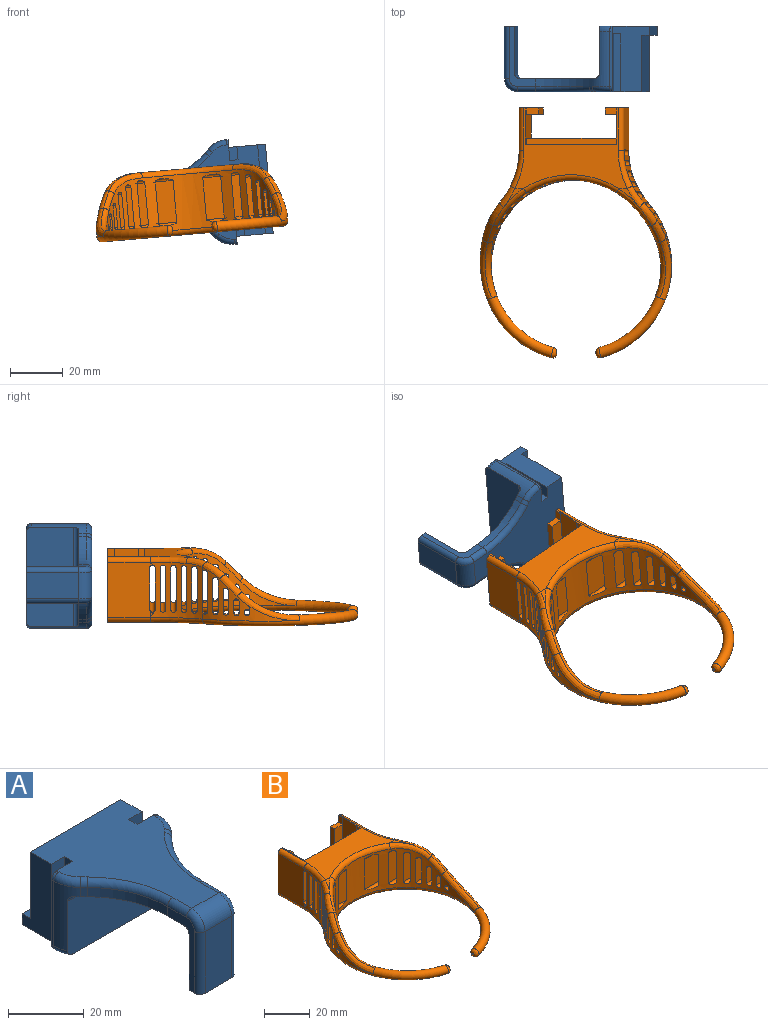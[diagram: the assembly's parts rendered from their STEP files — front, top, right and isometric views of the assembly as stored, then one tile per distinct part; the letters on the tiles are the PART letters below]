
ASSEMBLY  parts=2 mates=1
PART A: 61 faces, bbox 41.6x56.9x25.4 mm
  f0: plane 20x10mm, normal (0,-1,0), area 200mm2, adj f31,f34,f49,f50
  f1: plane 18x14mm, normal (0,1,0), area 252mm2, adj f2,f3,f31,f32
  f2: plane 23x10.07mm, normal (1,0,0), area 69.1mm2, adj f1,f6,f31,f32,f40,f47,f48,f49
  f3: plane 23x10.07mm, normal (-1,0,0), area 69.1mm2, adj f1,f6,f31,f32,f39,f50,f51,f52
  f4: plane 48.5x36mm, normal (0,0,1), area 1036.4mm2, adj f5,f7,f8,f10,f11,f12,f13,f14
  f5: plane 25x14.06mm, normal (-1,0,0), area 218.4mm2, adj f4,f8,f9,f12,f14,f18,f27,f28
  f6: plane 35.78x29.5mm, normal (0,0,-1), area 572.7mm2, adj f2,f3,f32,f33,f37,f38,f39,f40
  f7: plane 25x14.06mm, normal (1,0,0), area 218.4mm2, adj f4,f8,f9,f13,f15,f17,f27,f28
  f8: plane 34x21.5mm, normal (0,1,0), area 731mm2, adj f4,f5,f7,f27
  f9: plane 36x19mm, normal (0,0,-1), area 542.3mm2, adj f5,f7,f12,f13,f16,f19,f20,f21
  f10: plane 22x3.12mm, normal (1,0,0), area 68.6mm2, adj f4,f13,f15,f17
  f11: plane 22x3.12mm, normal (-1,0,0), area 68.6mm2, adj f4,f12,f14,f18
  f12: plane 25x8mm, normal (0,1,0), area 183.3mm2, adj f4,f5,f9,f11,f18,f36,f56,f58
  f13: plane 25x8mm, normal (0,1,0), area 183.3mm2, adj f4,f7,f9,f10,f17,f35,f43,f60
  f14: plane 22x5mm, normal (0,-1,0), area 110mm2, adj f4,f5,f11,f18
  f15: plane 22x5mm, normal (0,-1,0), area 110mm2, adj f4,f7,f10,f17
  f16: plane 38.2x18mm, normal (0,-1,0), area 685.8mm2, adj f9,f33,f41,f42,f57,f59
  f17: plane 5x3.12mm, normal (0,0,1), area 15.6mm2, adj f7,f10,f13,f15
  f18: plane 5x3.12mm, normal (0,0,1), area 15.6mm2, adj f5,f11,f12,f14
  f19: plane 22x18mm, normal (0,-1,0), area 396mm2, adj f9,f20,f22,f29
  f20: plane 22x3.12mm, normal (1,0,0), area 68.6mm2, adj f9,f19,f21,f29
  f21: plane 22x18mm, normal (0,1,0), area 396mm2, adj f9,f20,f22,f29
  f22: plane 22x3.12mm, normal (-1,0,0), area 68.6mm2, adj f9,f19,f21,f29
  f23: plane 28x22mm, normal (0,-1,0), area 616mm2, adj f9,f24,f26,f30
  f24: plane 22x1.94mm, normal (1,0,0), area 42.7mm2, adj f9,f23,f25,f30
  f25: plane 28x22mm, normal (0,1,0), area 616mm2, adj f9,f24,f26,f30
  f26: plane 22x1.94mm, normal (-1,0,0), area 42.7mm2, adj f9,f23,f25,f30
  f27: plane 34x3mm, normal (0,0,1), area 102mm2, adj f5,f7,f8,f28
  f28: plane 34x3.5mm, normal (0,1,0), area 119mm2, adj f5,f7,f9,f27
  f29: plane 18x3.12mm, normal (0,0,-1), area 56.2mm2, adj f19,f20,f21,f22
  f30: plane 28x1.94mm, normal (0,0,-1), area 54.3mm2, adj f23,f24,f25,f26
  f31: plane 14x4mm, normal (0,0,-1), area 54.3mm2, adj f0,f1,f2,f3,f49,f50
  f32: cylinder r=2mm len=14mm, axis (-1,0,0), area 44mm2, adj f1,f2,f3,f6
  f33: cylinder r=2mm len=38.2mm, axis (1,0,0), area 117.5mm2, adj f6,f16,f41,f42
  f34: cylinder r=5mm len=10mm, axis (-1,0,0), area 78.5mm2, adj f0,f4,f48,f51
  f35: plane 21x0.8mm, normal (1,0,0), area 16.8mm2, adj f13,f42,f43,f60
  f36: plane 21x0.8mm, normal (-1,0,0), area 16.8mm2, adj f12,f41,f56,f58
  f37: plane 3x1.28mm, normal (0.71,-0.71,0), area 5.4mm2, adj f6,f40,f42,f45
  f38: plane 3x1.28mm, normal (-0.71,-0.71,0), area 5.4mm2, adj f6,f39,f41,f54
  f39: cylinder r=30mm len=21.21mm, axis (0,0,1), area 70.7mm2, adj f3,f6,f38,f53
  f40: cylinder r=30mm len=21.21mm, axis (0,0,-1), area 70.7mm2, adj f2,f6,f37,f46
  f41: cylinder r=10mm len=21mm, axis (0,0,-1), area 101.4mm2, adj f6,f16,f33,f36,f38,f55,f57
  f42: cylinder r=10mm len=21mm, axis (0,0,-1), area 101.4mm2, adj f6,f16,f33,f35,f37,f44,f59
  f43: cylinder r=2mm len=2mm, axis (0,-1,0), area 2.5mm2, adj f4,f13,f35,f44
  f44: torus R=8mm, axis (0,0,1), area 22.9mm2, adj f4,f42,f43,f45
  f45: cylinder r=2mm len=2.7mm, axis (0.71,0.71,0), area 5.7mm2, adj f4,f37,f44,f46
  f46: torus R=32mm, axis (0,0,1), area 75.8mm2, adj f4,f40,f45,f47
  f47: cylinder r=2mm len=7.07mm, axis (0,-1,0), area 22.2mm2, adj f2,f4,f46,f48
  f48: torus R=3mm, axis (1,0,0), area 21.1mm2, adj f2,f34,f47,f49
  f49: cylinder r=2mm len=20mm, axis (0,0,-1), area 62.8mm2, adj f0,f2,f31,f48
  f50: cylinder r=2mm len=20mm, axis (0,0,-1), area 62.8mm2, adj f0,f3,f31,f51
  f51: torus R=3mm, axis (-1,0,0), area 21.1mm2, adj f3,f34,f50,f52
  f52: cylinder r=2mm len=7.07mm, axis (0,-1,0), area 22.2mm2, adj f3,f4,f51,f53
  f53: torus R=32mm, axis (0,0,1), area 75.8mm2, adj f4,f39,f52,f54
  f54: cylinder r=2mm len=2.7mm, axis (0.71,-0.71,0), area 5.7mm2, adj f4,f38,f53,f55
  f55: torus R=8mm, axis (0,0,1), area 22.9mm2, adj f4,f41,f54,f56
  f56: cylinder r=2mm len=2mm, axis (0,-1,0), area 2.5mm2, adj f4,f12,f36,f55
  f57: torus R=8mm, axis (0,0,1), area 13.5mm2, adj f9,f16,f41,f58
  f58: cylinder r=2mm len=2mm, axis (0,-1,0), area 2.5mm2, adj f9,f12,f36,f57
  f59: torus R=8mm, axis (0,0,1), area 13.5mm2, adj f9,f16,f42,f60
  f60: cylinder r=2mm len=2mm, axis (0,-1,0), area 2.5mm2, adj f9,f13,f35,f59
PART B: 124 faces, bbox 79x98.1x25.1 mm
  f0: cylinder r=36.5mm len=37.21mm, axis (0,0,-1), area 194.9mm2, adj f7,f74,f75,f76,f77,f78,f79,f80
  f1: cylinder r=32.5mm len=65mm, axis (0,0,-1), area 1086.7mm2, adj f28,f29,f30,f31,f32,f33,f34,f35
  f2: cylinder r=36.5mm len=37.21mm, axis (0,0,-1), area 194.9mm2, adj f6,f56,f57,f58,f59,f60,f61,f62
  f3: plane 43.01x30.72mm, normal (0,0,1), area 521.3mm2, adj f8,f9,f10,f13,f15,f18,f19,f21
  f4: plane 0.83x0.8mm, normal (-1,0,0), area 0.5mm2, adj f119
  f5: plane 0.83x0.8mm, normal (1,0,0), area 0.5mm2, adj f118
  f6: cylinder r=30mm len=21mm, axis (0,0,-1), area 264.7mm2, adj f2,f16,f36,f37,f38,f39,f40,f41
  f7: cylinder r=30mm len=21mm, axis (0,0,-1), area 264.7mm2, adj f0,f17,f28,f29,f30,f31,f32,f33
  f8: plane 25x7.25mm, normal (0,1,0), area 162.2mm2, adj f3,f11,f14,f17,f22,f23,f94,f109
  f9: plane 35x25mm, normal (0,1,0), area 744.7mm2, adj f3,f14,f18,f19,f24,f25,f26
  f10: plane 25x4.75mm, normal (0,-1,0), area 101.4mm2, adj f3,f11,f14,f18,f22,f23
  f11: plane 21.25x2.5mm, normal (1,0,0), area 53.1mm2, adj f8,f10,f14,f22
  f12: plane 21.25x2.5mm, normal (-1,0,0), area 53.1mm2, adj f13,f14,f15,f20
  f13: plane 25x7.25mm, normal (0,1,0), area 162.2mm2, adj f3,f12,f14,f16,f20,f21,f101,f107
  f14: plane 51.88x37.25mm, normal (0,0,-1), area 645.1mm2, adj f8,f9,f10,f11,f12,f13,f15,f18
  f15: plane 25x4.75mm, normal (0,-1,0), area 101.4mm2, adj f3,f12,f14,f19,f20,f21
  f16: plane 21x16.16mm, normal (1,0,0), area 336.7mm2, adj f6,f13,f44,f45,f47,f101,f107
  f17: plane 21x16.16mm, normal (-1,0,0), area 336.7mm2, adj f7,f8,f44,f45,f47,f94,f109
  f18: plane 25x9mm, normal (1,0,0), area 225mm2, adj f3,f9,f10,f14
  f19: plane 25x9mm, normal (-1,0,0), area 225mm2, adj f3,f9,f14,f15
  f20: plane 4.63x2.5mm, normal (0,0,1), area 11.6mm2, adj f12,f13,f15,f21
  f21: plane 3.75x2.5mm, normal (-1,0,0), area 9.4mm2, adj f3,f13,f15,f20
  f22: plane 4.63x2.5mm, normal (0,0,1), area 11.6mm2, adj f8,f10,f11,f23
  f23: plane 3.75x2.5mm, normal (1,0,0), area 9.4mm2, adj f3,f8,f10,f22
  f24: plane 34.75x2.5mm, normal (0,0,1), area 86.9mm2, adj f9,f25,f26,f27
  f25: plane 3.75x2.5mm, normal (1,0,0), area 9.4mm2, adj f3,f9,f24,f27
  f26: plane 3.75x2.5mm, normal (-1,0,0), area 9.4mm2, adj f3,f9,f24,f27
  f27: plane 34.75x3.75mm, normal (0,1,0), area 130.3mm2, adj f3,f24,f25,f26
  f28: cylinder r=1mm len=9.38mm, axis (1,0,0), area 22.6mm2, adj f1,f7,f29,f31
  f29: plane 16x8.03mm, normal (0,-1,0), area 128.4mm2, adj f1,f7,f28,f30
  f30: cylinder r=1mm len=9.38mm, axis (1,0,0), area 22.6mm2, adj f1,f7,f29,f31
  f31: plane 16x6.38mm, normal (0,1,0), area 102.1mm2, adj f1,f7,f28,f30
  f32: plane 16.76x16mm, normal (0,-1,0), area 268.1mm2, adj f1,f7,f33,f35
  f33: cylinder r=1mm len=17.71mm, axis (1,0,0), area 43.4mm2, adj f1,f7,f32,f34
  f34: plane 16x10.89mm, normal (0,1,0), area 174.2mm2, adj f1,f7,f33,f35
  f35: cylinder r=1mm len=17.71mm, axis (1,0,0), area 43.4mm2, adj f1,f7,f32,f34
  f36: plane 43.32x16mm, normal (0,1,0), area 693.1mm2, adj f6,f7,f37,f39
  f37: cylinder r=1mm len=43.32mm, axis (1,0,0), area 134.2mm2, adj f6,f7,f36,f38
  f38: plane 42.09x16mm, normal (0,-1,0), area 673.4mm2, adj f6,f7,f37,f39
  f39: cylinder r=1mm len=43.32mm, axis (1,0,0), area 134.2mm2, adj f6,f7,f36,f38
  f40: cylinder r=1mm len=41.15mm, axis (1,0,0), area 128.2mm2, adj f6,f7,f41,f43
  f41: plane 41.15x16mm, normal (0,1,0), area 658.4mm2, adj f6,f7,f40,f42
  f42: cylinder r=1mm len=41.15mm, axis (1,0,0), area 128.2mm2, adj f6,f7,f41,f43
  f43: plane 40.49x16mm, normal (0,-1,0), area 647.9mm2, adj f6,f7,f40,f42
  f44: plane 40x16mm, normal (0,-1,0), area 640mm2, adj f16,f17,f45,f47
  f45: cylinder r=1mm len=40.11mm, axis (1,0,0), area 125.8mm2, adj f6,f7,f16,f17,f44,f46
  f46: plane 40.11x16mm, normal (0,1,0), area 641.8mm2, adj f6,f7,f45,f47
  f47: cylinder r=1mm len=40.11mm, axis (1,0,0), area 125.8mm2, adj f6,f7,f16,f17,f44,f46
  f48: plane 16x6.38mm, normal (0,1,0), area 102.1mm2, adj f1,f6,f49,f51
  f49: cylinder r=1mm len=9.38mm, axis (1,0,0), area 22.6mm2, adj f1,f6,f48,f50
  f50: plane 16x8.03mm, normal (0,-1,0), area 128.4mm2, adj f1,f6,f49,f51
  f51: cylinder r=1mm len=9.38mm, axis (1,0,0), area 22.6mm2, adj f1,f6,f48,f50
  f52: cylinder r=1mm len=17.71mm, axis (1,0,0), area 43.4mm2, adj f1,f6,f53,f55
  f53: plane 16x10.89mm, normal (0,1,0), area 174.2mm2, adj f1,f6,f52,f54
  f54: cylinder r=1mm len=17.71mm, axis (1,0,0), area 43.4mm2, adj f1,f6,f53,f55
  f55: plane 16.76x16mm, normal (0,-1,0), area 268.1mm2, adj f1,f6,f52,f54
  f56: plane 4.11x0.34mm, normal (0,-1,0), area 1.4mm2, adj f1,f2,f120,f121
  f57: plane 4.06x0.34mm, normal (0,1,0), area 1.4mm2, adj f1,f2,f120,f121
  f58: plane 4.34x4.18mm, normal (0,1,0), area 18.2mm2, adj f1,f2,f59,f61
  f59: cylinder r=1mm len=4.9mm, axis (1,0,0), area 13.3mm2, adj f1,f2,f58,f60
  f60: plane 4.34x4.27mm, normal (0,-1,0), area 18.5mm2, adj f1,f2,f59,f61
  f61: cylinder r=1mm len=4.9mm, axis (1,0,0), area 13.3mm2, adj f1,f2,f58,f60
  f62: plane 8.34x4.52mm, normal (0,-1,0), area 37.7mm2, adj f1,f2,f63,f65
  f63: cylinder r=1mm len=5.42mm, axis (1,0,0), area 14mm2, adj f1,f2,f62,f64
  f64: plane 8.34x4.38mm, normal (0,1,0), area 36.5mm2, adj f1,f2,f63,f65
  f65: cylinder r=1mm len=5.42mm, axis (1,0,0), area 14mm2, adj f1,f2,f62,f64
  f66: cylinder r=1mm len=6.14mm, axis (1,0,0), area 15.1mm2, adj f1,f2,f67,f69
  f67: plane 12.34x4.92mm, normal (0,-1,0), area 60.7mm2, adj f1,f2,f66,f68
  f68: cylinder r=1mm len=6.14mm, axis (1,0,0), area 15.1mm2, adj f1,f2,f67,f69
  f69: plane 12.34x4.69mm, normal (0,1,0), area 57.9mm2, adj f1,f2,f66,f68
  f70: plane 14.81x5.59mm, normal (0,-1,0), area 82.7mm2, adj f1,f2,f71,f73
  f71: cylinder r=1mm len=7.21mm, axis (1,0,0), area 16.9mm2, adj f1,f2,f70,f72
  f72: plane 14.81x5.2mm, normal (0,1,0), area 77.1mm2, adj f1,f2,f71,f73
  f73: cylinder r=1mm len=7.21mm, axis (1,0,0), area 16.9mm2, adj f1,f2,f70,f72
  f74: plane 4.06x0.34mm, normal (0,1,0), area 1.4mm2, adj f0,f1,f122,f123
  f75: plane 4.11x0.34mm, normal (0,-1,0), area 1.4mm2, adj f0,f1,f122,f123
  f76: cylinder r=1mm len=4.9mm, axis (1,0,0), area 13.3mm2, adj f0,f1,f77,f79
  f77: plane 4.34x4.27mm, normal (0,-1,0), area 18.5mm2, adj f0,f1,f76,f78
  f78: cylinder r=1mm len=4.9mm, axis (1,0,0), area 13.3mm2, adj f0,f1,f77,f79
  f79: plane 4.34x4.18mm, normal (0,1,0), area 18.2mm2, adj f0,f1,f76,f78
  f80: cylinder r=1mm len=5.42mm, axis (1,0,0), area 14mm2, adj f0,f1,f81,f83
  f81: plane 8.34x4.38mm, normal (0,1,0), area 36.5mm2, adj f0,f1,f80,f82
  f82: cylinder r=1mm len=5.42mm, axis (1,0,0), area 14mm2, adj f0,f1,f81,f83
  f83: plane 8.34x4.52mm, normal (0,-1,0), area 37.7mm2, adj f0,f1,f80,f82
  f84: plane 12.34x4.69mm, normal (0,1,0), area 57.9mm2, adj f0,f1,f85,f87
  f85: cylinder r=1mm len=6.14mm, axis (1,0,0), area 15.1mm2, adj f0,f1,f84,f86
  f86: plane 12.34x4.92mm, normal (0,-1,0), area 60.7mm2, adj f0,f1,f85,f87
  f87: cylinder r=1mm len=6.14mm, axis (1,0,0), area 15.1mm2, adj f0,f1,f84,f86
  f88: cylinder r=1mm len=7.21mm, axis (1,0,0), area 16.9mm2, adj f0,f1,f89,f91
  f89: plane 14.81x5.2mm, normal (0,1,0), area 77.1mm2, adj f0,f1,f88,f90
  f90: cylinder r=1mm len=7.21mm, axis (1,0,0), area 16.9mm2, adj f0,f1,f89,f91
  f91: plane 14.81x5.59mm, normal (0,-1,0), area 82.7mm2, adj f0,f1,f88,f90
  f92: cylinder r=20mm len=7.7mm, axis (-1,0,0), area 12.1mm2, adj f3,f103,f115
  f93: cylinder r=20mm len=7.7mm, axis (-1,0,0), area 12.1mm2, adj f3,f96,f113
  f94: cylinder r=2mm len=16.16mm, axis (0,1,0), area 50.8mm2, adj f3,f8,f17,f95
  f95: torus R=32mm, axis (0,0,1), area 45.6mm2, adj f3,f7,f94,f96
  f96: bspline ~12.27x9.35mm, area 27.4mm2, adj f7,f93,f95,f97
  f97: bspline ~12.56x9.76mm, area 35.5mm2, adj f0,f96,f98,f113
  f98: bspline ~13.57x13.34mm, area 35.5mm2, adj f0,f97,f99,f112
  f99: bspline ~29.8x13.81mm, area 81.3mm2, adj f0,f98,f100,f111
  f100: torus R=34.5mm, axis (0,0,1), area 1460.8mm2, adj f0,f1,f2,f14,f99,f106,f108,f110
  f101: cylinder r=2mm len=16.16mm, axis (0,-1,0), area 50.8mm2, adj f3,f13,f16,f102
  f102: torus R=32mm, axis (0,0,1), area 45.6mm2, adj f3,f6,f101,f103
  f103: bspline ~12.27x9.35mm, area 27.4mm2, adj f6,f92,f102,f104
  f104: bspline ~12.56x9.76mm, area 35.5mm2, adj f2,f103,f105,f115
  f105: bspline ~13.57x13.34mm, area 35.5mm2, adj f2,f104,f106,f116
  f106: bspline ~27.92x11.79mm, area 81.3mm2, adj f2,f100,f105,f117
  f107: cylinder r=2mm len=16.16mm, axis (0,1,0), area 50.8mm2, adj f13,f14,f16,f108
  f108: torus R=32mm, axis (0,0,1), area 69.5mm2, adj f6,f14,f100,f107
  f109: cylinder r=2mm len=16.16mm, axis (0,-1,0), area 50.8mm2, adj f8,f14,f17,f110
  f110: torus R=32mm, axis (0,0,1), area 69.5mm2, adj f7,f14,f100,f109
  f111: bspline ~25.56x11.4mm, area 73.1mm2, adj f1,f99,f100,f112
  f112: bspline ~7.77x6.84mm, area 23.8mm2, adj f1,f98,f111,f113
  f113: bspline ~17.77x16.91mm, area 51.8mm2, adj f1,f93,f97,f112,f114
  f114: torus R=34.5mm, axis (0,0,1), area 116.3mm2, adj f1,f3,f113,f115
  f115: bspline ~17.77x16.91mm, area 51.8mm2, adj f1,f92,f104,f114,f116
  f116: bspline ~7.77x6.84mm, area 23.8mm2, adj f1,f105,f115,f117
  f117: bspline ~27.24x13.32mm, area 73.1mm2, adj f1,f100,f106,f116
  f118: bspline ~4x3.96mm, area 22.5mm2, adj f5,f100
  f119: bspline ~4x3.96mm, area 22.5mm2, adj f4,f100
  f120: cylinder r=1mm len=4.5mm, axis (1,0,0), area 12.8mm2, adj f1,f2,f56,f57
  f121: cylinder r=1mm len=4.5mm, axis (-1,0,0), area 12.8mm2, adj f1,f2,f56,f57
  f122: cylinder r=1mm len=4.5mm, axis (1,0,0), area 12.8mm2, adj f0,f1,f74,f75
  f123: cylinder r=1mm len=4.5mm, axis (-1,0,0), area 12.8mm2, adj f0,f1,f74,f75
PLACE A rot(axis=(0.61,0.56,-0.56),117.2deg) t=(-7.44,14.22,15.72)mm
PLACE B rot(axis=(0,-1,0),5deg) t=(-18.68,-23.93,0)mm
MATE parallel A.f7 <-> B.f14  axis (0.09,0,-1) through (5.06,2.71,-0.25)mm
